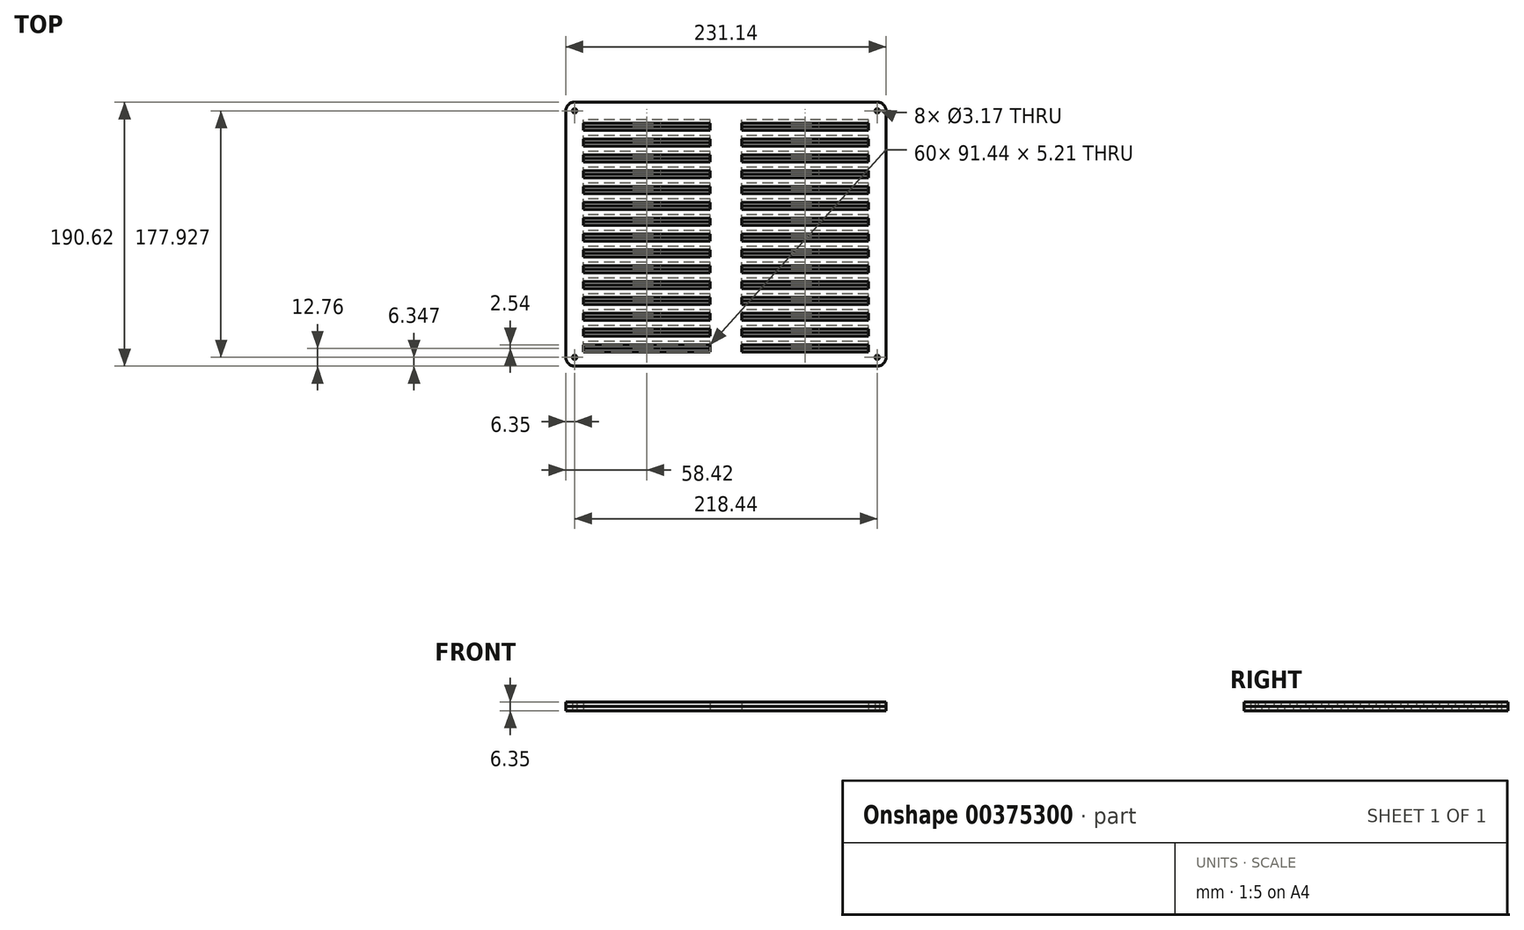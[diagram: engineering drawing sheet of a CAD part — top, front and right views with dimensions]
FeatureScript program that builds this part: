
annotation { "Feature Type Name" : "Feature", "Feature Type Description" : "" }
export const myFeature = defineFeature(function(context is Context, id is Id, definition is map)
    precondition{}
    {
        {
            var Q0;
            Q0=qCreatedBy(makeId("Top.planeOp"),FACE);
            var sketch = newSketch(context, id + "F0", { "sketchPlane" : qUnion([Q0])});
            skLineSegment(sketch, "E0.bottom", {"start": v(45.72, -2.6) * mm, "end": v(-45.72, -2.6) * mm});
            skLineSegment(sketch, "E0.top", {"start": v(45.72, 2.6) * mm, "end": v(-45.72, 2.6) * mm});
            skLineSegment(sketch, "E0.left", {"start": v(45.72, -2.6) * mm, "end": v(45.72, 2.6) * mm});
            skLineSegment(sketch, "E0.right", {"start": v(-45.72, -2.6) * mm, "end": v(-45.72, 2.6) * mm});
            skPoint(sketch, "E0.middle", {"position": v(0, 0) * mm});
            skLineSegment(sketch, "E1", {"start": v(0, 0) * mm, "end": v(0, 156.34) * mm, "construction": true});
            skLineSegment(sketch, "E2", {"start": v(0, 0) * mm, "end": v(0, -142.64) * mm, "construction": true});
            skPoint(sketch, "E3.0.1.0", {"position": v(0, 11.43) * mm});
            skLineSegment(sketch, "E3.0.1.1", {"start": v(45.72, 8.83) * mm, "end": v(-45.72, 8.83) * mm});
            skLineSegment(sketch, "E3.0.1.2", {"start": v(45.72, 14.03) * mm, "end": v(-45.72, 14.03) * mm});
            skLineSegment(sketch, "E3.0.1.3", {"start": v(45.72, 8.83) * mm, "end": v(45.72, 14.03) * mm});
            skLineSegment(sketch, "E3.0.1.4", {"start": v(-45.72, 8.83) * mm, "end": v(-45.72, 14.03) * mm});
            skPoint(sketch, "E3.0.2.0", {"position": v(0, 22.86) * mm});
            skLineSegment(sketch, "E3.0.2.1", {"start": v(45.72, 20.26) * mm, "end": v(-45.72, 20.26) * mm});
            skLineSegment(sketch, "E3.0.2.2", {"start": v(45.72, 25.46) * mm, "end": v(-45.72, 25.46) * mm});
            skLineSegment(sketch, "E3.0.2.3", {"start": v(45.72, 20.26) * mm, "end": v(45.72, 25.46) * mm});
            skLineSegment(sketch, "E3.0.2.4", {"start": v(-45.72, 20.26) * mm, "end": v(-45.72, 25.46) * mm});
            skPoint(sketch, "E3.0.3.0", {"position": v(0, 34.29) * mm});
            skLineSegment(sketch, "E3.0.3.1", {"start": v(45.72, 31.69) * mm, "end": v(-45.72, 31.69) * mm});
            skLineSegment(sketch, "E3.0.3.2", {"start": v(45.72, 36.9) * mm, "end": v(-45.72, 36.9) * mm});
            skLineSegment(sketch, "E3.0.3.3", {"start": v(45.72, 31.69) * mm, "end": v(45.72, 36.9) * mm});
            skLineSegment(sketch, "E3.0.3.4", {"start": v(-45.72, 31.69) * mm, "end": v(-45.72, 36.9) * mm});
            skPoint(sketch, "E3.0.4.0", {"position": v(0, 45.72) * mm});
            skLineSegment(sketch, "E3.0.4.1", {"start": v(45.72, 43.12) * mm, "end": v(-45.72, 43.12) * mm});
            skLineSegment(sketch, "E3.0.4.2", {"start": v(45.72, 48.32) * mm, "end": v(-45.72, 48.32) * mm});
            skLineSegment(sketch, "E3.0.4.3", {"start": v(45.72, 43.12) * mm, "end": v(45.72, 48.32) * mm});
            skLineSegment(sketch, "E3.0.4.4", {"start": v(-45.72, 43.12) * mm, "end": v(-45.72, 48.32) * mm});
            skPoint(sketch, "E3.0.5.0", {"position": v(0, 57.15) * mm});
            skLineSegment(sketch, "E3.0.5.1", {"start": v(45.72, 54.55) * mm, "end": v(-45.72, 54.55) * mm});
            skLineSegment(sketch, "E3.0.5.2", {"start": v(45.72, 59.75) * mm, "end": v(-45.72, 59.75) * mm});
            skLineSegment(sketch, "E3.0.5.3", {"start": v(45.72, 54.55) * mm, "end": v(45.72, 59.75) * mm});
            skLineSegment(sketch, "E3.0.5.4", {"start": v(-45.72, 54.55) * mm, "end": v(-45.72, 59.75) * mm});
            skPoint(sketch, "E3.0.6.0", {"position": v(0, 68.58) * mm});
            skLineSegment(sketch, "E3.0.6.1", {"start": v(45.72, 65.98) * mm, "end": v(-45.72, 65.98) * mm});
            skLineSegment(sketch, "E3.0.6.2", {"start": v(45.72, 71.18) * mm, "end": v(-45.72, 71.18) * mm});
            skLineSegment(sketch, "E3.0.6.3", {"start": v(45.72, 65.98) * mm, "end": v(45.72, 71.18) * mm});
            skLineSegment(sketch, "E3.0.6.4", {"start": v(-45.72, 65.98) * mm, "end": v(-45.72, 71.18) * mm});
            skPoint(sketch, "E3.0.7.0", {"position": v(0, 80) * mm});
            skLineSegment(sketch, "E3.0.7.1", {"start": v(45.72, 77.4) * mm, "end": v(-45.72, 77.4) * mm});
            skLineSegment(sketch, "E3.0.7.2", {"start": v(45.72, 82.61) * mm, "end": v(-45.72, 82.61) * mm});
            skLineSegment(sketch, "E3.0.7.3", {"start": v(45.72, 77.4) * mm, "end": v(45.72, 82.61) * mm});
            skLineSegment(sketch, "E3.0.7.4", {"start": v(-45.72, 77.4) * mm, "end": v(-45.72, 82.61) * mm});
            skPoint(sketch, "E3.0.8.0", {"position": v(0, 91.44) * mm});
            skLineSegment(sketch, "E3.0.8.1", {"start": v(45.72, 88.84) * mm, "end": v(-45.72, 88.84) * mm});
            skLineSegment(sketch, "E3.0.8.2", {"start": v(45.72, 94.04) * mm, "end": v(-45.72, 94.04) * mm});
            skLineSegment(sketch, "E3.0.8.3", {"start": v(45.72, 88.84) * mm, "end": v(45.72, 94.04) * mm});
            skLineSegment(sketch, "E3.0.8.4", {"start": v(-45.72, 88.84) * mm, "end": v(-45.72, 94.04) * mm});
            skPoint(sketch, "E3.0.9.0", {"position": v(0, 102.87) * mm});
            skLineSegment(sketch, "E3.0.9.1", {"start": v(45.72, 100.27) * mm, "end": v(-45.72, 100.27) * mm});
            skLineSegment(sketch, "E3.0.9.2", {"start": v(45.72, 105.47) * mm, "end": v(-45.72, 105.47) * mm});
            skLineSegment(sketch, "E3.0.9.3", {"start": v(45.72, 100.27) * mm, "end": v(45.72, 105.47) * mm});
            skLineSegment(sketch, "E3.0.9.4", {"start": v(-45.72, 100.27) * mm, "end": v(-45.72, 105.47) * mm});
            skPoint(sketch, "E3.0.10.0", {"position": v(0, 114.3) * mm});
            skLineSegment(sketch, "E3.0.10.1", {"start": v(45.72, 111.7) * mm, "end": v(-45.72, 111.7) * mm});
            skLineSegment(sketch, "E3.0.10.2", {"start": v(45.72, 116.9) * mm, "end": v(-45.72, 116.9) * mm});
            skLineSegment(sketch, "E3.0.10.3", {"start": v(45.72, 111.7) * mm, "end": v(45.72, 116.9) * mm});
            skLineSegment(sketch, "E3.0.10.4", {"start": v(-45.72, 111.7) * mm, "end": v(-45.72, 116.9) * mm});
            skPoint(sketch, "E3.0.11.0", {"position": v(0, 125.73) * mm});
            skLineSegment(sketch, "E3.0.11.1", {"start": v(45.72, 123.13) * mm, "end": v(-45.72, 123.13) * mm});
            skLineSegment(sketch, "E3.0.11.2", {"start": v(45.72, 128.33) * mm, "end": v(-45.72, 128.33) * mm});
            skLineSegment(sketch, "E3.0.11.3", {"start": v(45.72, 123.13) * mm, "end": v(45.72, 128.33) * mm});
            skLineSegment(sketch, "E3.0.11.4", {"start": v(-45.72, 123.13) * mm, "end": v(-45.72, 128.33) * mm});
            skPoint(sketch, "E3.0.12.0", {"position": v(0, 137.16) * mm});
            skLineSegment(sketch, "E3.0.12.1", {"start": v(45.72, 134.56) * mm, "end": v(-45.72, 134.56) * mm});
            skLineSegment(sketch, "E3.0.12.2", {"start": v(45.72, 139.76) * mm, "end": v(-45.72, 139.76) * mm});
            skLineSegment(sketch, "E3.0.12.3", {"start": v(45.72, 134.56) * mm, "end": v(45.72, 139.76) * mm});
            skLineSegment(sketch, "E3.0.12.4", {"start": v(-45.72, 134.56) * mm, "end": v(-45.72, 139.76) * mm});
            skPoint(sketch, "E3.0.13.0", {"position": v(0, 148.59) * mm});
            skLineSegment(sketch, "E3.0.13.1", {"start": v(45.72, 145.99) * mm, "end": v(-45.72, 145.99) * mm});
            skLineSegment(sketch, "E3.0.13.2", {"start": v(45.72, 151.2) * mm, "end": v(-45.72, 151.2) * mm});
            skLineSegment(sketch, "E3.0.13.3", {"start": v(45.72, 145.99) * mm, "end": v(45.72, 151.2) * mm});
            skLineSegment(sketch, "E3.0.13.4", {"start": v(-45.72, 145.99) * mm, "end": v(-45.72, 151.2) * mm});
            skPoint(sketch, "E3.0.14.0", {"position": v(0, 160.02) * mm});
            skLineSegment(sketch, "E3.0.14.1", {"start": v(45.72, 157.42) * mm, "end": v(-45.72, 157.42) * mm});
            skLineSegment(sketch, "E3.0.14.2", {"start": v(45.72, 162.62) * mm, "end": v(-45.72, 162.62) * mm});
            skLineSegment(sketch, "E3.0.14.3", {"start": v(45.72, 157.42) * mm, "end": v(45.72, 162.62) * mm});
            skLineSegment(sketch, "E3.0.14.4", {"start": v(-45.72, 157.42) * mm, "end": v(-45.72, 162.62) * mm});
            skPoint(sketch, "E3.1.0.0", {"position": v(114.3, 0) * mm});
            skLineSegment(sketch, "E3.1.0.1", {"start": v(160.02, -2.6) * mm, "end": v(68.58, -2.6) * mm});
            skLineSegment(sketch, "E3.1.0.2", {"start": v(160.02, 2.6) * mm, "end": v(68.58, 2.6) * mm});
            skLineSegment(sketch, "E3.1.0.3", {"start": v(160.02, -2.6) * mm, "end": v(160.02, 2.6) * mm});
            skLineSegment(sketch, "E3.1.0.4", {"start": v(68.58, -2.6) * mm, "end": v(68.58, 2.6) * mm});
            skPoint(sketch, "E3.1.1.0", {"position": v(114.3, 11.43) * mm});
            skLineSegment(sketch, "E3.1.1.1", {"start": v(160.02, 8.83) * mm, "end": v(68.58, 8.83) * mm});
            skLineSegment(sketch, "E3.1.1.2", {"start": v(160.02, 14.03) * mm, "end": v(68.58, 14.03) * mm});
            skLineSegment(sketch, "E3.1.1.3", {"start": v(160.02, 8.83) * mm, "end": v(160.02, 14.03) * mm});
            skLineSegment(sketch, "E3.1.1.4", {"start": v(68.58, 8.83) * mm, "end": v(68.58, 14.03) * mm});
            skPoint(sketch, "E3.1.2.0", {"position": v(114.3, 22.86) * mm});
            skLineSegment(sketch, "E3.1.2.1", {"start": v(160.02, 20.26) * mm, "end": v(68.58, 20.26) * mm});
            skLineSegment(sketch, "E3.1.2.2", {"start": v(160.02, 25.46) * mm, "end": v(68.58, 25.46) * mm});
            skLineSegment(sketch, "E3.1.2.3", {"start": v(160.02, 20.26) * mm, "end": v(160.02, 25.46) * mm});
            skLineSegment(sketch, "E3.1.2.4", {"start": v(68.58, 20.26) * mm, "end": v(68.58, 25.46) * mm});
            skPoint(sketch, "E3.1.3.0", {"position": v(114.3, 34.29) * mm});
            skLineSegment(sketch, "E3.1.3.1", {"start": v(160.02, 31.69) * mm, "end": v(68.58, 31.69) * mm});
            skLineSegment(sketch, "E3.1.3.2", {"start": v(160.02, 36.9) * mm, "end": v(68.58, 36.9) * mm});
            skLineSegment(sketch, "E3.1.3.3", {"start": v(160.02, 31.69) * mm, "end": v(160.02, 36.9) * mm});
            skLineSegment(sketch, "E3.1.3.4", {"start": v(68.58, 31.69) * mm, "end": v(68.58, 36.9) * mm});
            skPoint(sketch, "E3.1.4.0", {"position": v(114.3, 45.72) * mm});
            skLineSegment(sketch, "E3.1.4.1", {"start": v(160.02, 43.12) * mm, "end": v(68.58, 43.12) * mm});
            skLineSegment(sketch, "E3.1.4.2", {"start": v(160.02, 48.32) * mm, "end": v(68.58, 48.32) * mm});
            skLineSegment(sketch, "E3.1.4.3", {"start": v(160.02, 43.12) * mm, "end": v(160.02, 48.32) * mm});
            skLineSegment(sketch, "E3.1.4.4", {"start": v(68.58, 43.12) * mm, "end": v(68.58, 48.32) * mm});
            skPoint(sketch, "E3.1.5.0", {"position": v(114.3, 57.15) * mm});
            skLineSegment(sketch, "E3.1.5.1", {"start": v(160.02, 54.55) * mm, "end": v(68.58, 54.55) * mm});
            skLineSegment(sketch, "E3.1.5.2", {"start": v(160.02, 59.75) * mm, "end": v(68.58, 59.75) * mm});
            skLineSegment(sketch, "E3.1.5.3", {"start": v(160.02, 54.55) * mm, "end": v(160.02, 59.75) * mm});
            skLineSegment(sketch, "E3.1.5.4", {"start": v(68.58, 54.55) * mm, "end": v(68.58, 59.75) * mm});
            skPoint(sketch, "E3.1.6.0", {"position": v(114.3, 68.58) * mm});
            skLineSegment(sketch, "E3.1.6.1", {"start": v(160.02, 65.98) * mm, "end": v(68.58, 65.98) * mm});
            skLineSegment(sketch, "E3.1.6.2", {"start": v(160.02, 71.18) * mm, "end": v(68.58, 71.18) * mm});
            skLineSegment(sketch, "E3.1.6.3", {"start": v(160.02, 65.98) * mm, "end": v(160.02, 71.18) * mm});
            skLineSegment(sketch, "E3.1.6.4", {"start": v(68.58, 65.98) * mm, "end": v(68.58, 71.18) * mm});
            skPoint(sketch, "E3.1.7.0", {"position": v(114.3, 80) * mm});
            skLineSegment(sketch, "E3.1.7.1", {"start": v(160.02, 77.4) * mm, "end": v(68.58, 77.4) * mm});
            skLineSegment(sketch, "E3.1.7.2", {"start": v(160.02, 82.61) * mm, "end": v(68.58, 82.61) * mm});
            skLineSegment(sketch, "E3.1.7.3", {"start": v(160.02, 77.4) * mm, "end": v(160.02, 82.61) * mm});
            skLineSegment(sketch, "E3.1.7.4", {"start": v(68.58, 77.4) * mm, "end": v(68.58, 82.61) * mm});
            skPoint(sketch, "E3.1.8.0", {"position": v(114.3, 91.44) * mm});
            skLineSegment(sketch, "E3.1.8.1", {"start": v(160.02, 88.84) * mm, "end": v(68.58, 88.84) * mm});
            skLineSegment(sketch, "E3.1.8.2", {"start": v(160.02, 94.04) * mm, "end": v(68.58, 94.04) * mm});
            skLineSegment(sketch, "E3.1.8.3", {"start": v(160.02, 88.84) * mm, "end": v(160.02, 94.04) * mm});
            skLineSegment(sketch, "E3.1.8.4", {"start": v(68.58, 88.84) * mm, "end": v(68.58, 94.04) * mm});
            skPoint(sketch, "E3.1.9.0", {"position": v(114.3, 102.87) * mm});
            skLineSegment(sketch, "E3.1.9.1", {"start": v(160.02, 100.27) * mm, "end": v(68.58, 100.27) * mm});
            skLineSegment(sketch, "E3.1.9.2", {"start": v(160.02, 105.47) * mm, "end": v(68.58, 105.47) * mm});
            skLineSegment(sketch, "E3.1.9.3", {"start": v(160.02, 100.27) * mm, "end": v(160.02, 105.47) * mm});
            skLineSegment(sketch, "E3.1.9.4", {"start": v(68.58, 100.27) * mm, "end": v(68.58, 105.47) * mm});
            skPoint(sketch, "E3.1.10.0", {"position": v(114.3, 114.3) * mm});
            skLineSegment(sketch, "E3.1.10.1", {"start": v(160.02, 111.7) * mm, "end": v(68.58, 111.7) * mm});
            skLineSegment(sketch, "E3.1.10.2", {"start": v(160.02, 116.9) * mm, "end": v(68.58, 116.9) * mm});
            skLineSegment(sketch, "E3.1.10.3", {"start": v(160.02, 111.7) * mm, "end": v(160.02, 116.9) * mm});
            skLineSegment(sketch, "E3.1.10.4", {"start": v(68.58, 111.7) * mm, "end": v(68.58, 116.9) * mm});
            skPoint(sketch, "E3.1.11.0", {"position": v(114.3, 125.73) * mm});
            skLineSegment(sketch, "E3.1.11.1", {"start": v(160.02, 123.13) * mm, "end": v(68.58, 123.13) * mm});
            skLineSegment(sketch, "E3.1.11.2", {"start": v(160.02, 128.33) * mm, "end": v(68.58, 128.33) * mm});
            skLineSegment(sketch, "E3.1.11.3", {"start": v(160.02, 123.13) * mm, "end": v(160.02, 128.33) * mm});
            skLineSegment(sketch, "E3.1.11.4", {"start": v(68.58, 123.13) * mm, "end": v(68.58, 128.33) * mm});
            skPoint(sketch, "E3.1.12.0", {"position": v(114.3, 137.16) * mm});
            skLineSegment(sketch, "E3.1.12.1", {"start": v(160.02, 134.56) * mm, "end": v(68.58, 134.56) * mm});
            skLineSegment(sketch, "E3.1.12.2", {"start": v(160.02, 139.76) * mm, "end": v(68.58, 139.76) * mm});
            skLineSegment(sketch, "E3.1.12.3", {"start": v(160.02, 134.56) * mm, "end": v(160.02, 139.76) * mm});
            skLineSegment(sketch, "E3.1.12.4", {"start": v(68.58, 134.56) * mm, "end": v(68.58, 139.76) * mm});
            skPoint(sketch, "E3.1.13.0", {"position": v(114.3, 148.59) * mm});
            skLineSegment(sketch, "E3.1.13.1", {"start": v(160.02, 145.99) * mm, "end": v(68.58, 145.99) * mm});
            skLineSegment(sketch, "E3.1.13.2", {"start": v(160.02, 151.2) * mm, "end": v(68.58, 151.2) * mm});
            skLineSegment(sketch, "E3.1.13.3", {"start": v(160.02, 145.99) * mm, "end": v(160.02, 151.2) * mm});
            skLineSegment(sketch, "E3.1.13.4", {"start": v(68.58, 145.99) * mm, "end": v(68.58, 151.2) * mm});
            skPoint(sketch, "E3.1.14.0", {"position": v(114.3, 160.02) * mm});
            skLineSegment(sketch, "E3.1.14.1", {"start": v(160.02, 157.42) * mm, "end": v(68.58, 157.42) * mm});
            skLineSegment(sketch, "E3.1.14.2", {"start": v(160.02, 162.62) * mm, "end": v(68.58, 162.62) * mm});
            skLineSegment(sketch, "E3.1.14.3", {"start": v(160.02, 157.42) * mm, "end": v(160.02, 162.62) * mm});
            skLineSegment(sketch, "E3.1.14.4", {"start": v(68.58, 157.42) * mm, "end": v(68.58, 162.62) * mm});
            skLineSegment(sketch, "E3.direction1", {"start": v(-45.72, -2.6) * mm, "end": v(68.58, -2.6) * mm, "construction": true});
            skLineSegment(sketch, "E3.direction2", {"start": v(-45.72, -2.6) * mm, "end": v(-45.72, 8.83) * mm, "construction": true});
            skLineSegment(sketch, "E4.bottom", {"start": v(-45.72, -2.6) * mm, "end": v(160.02, -2.6) * mm, "construction": true});
            skLineSegment(sketch, "E4.top", {"start": v(-45.72, 162.62) * mm, "end": v(160.02, 162.62) * mm, "construction": true});
            skLineSegment(sketch, "E4.left", {"start": v(-45.72, -2.6) * mm, "end": v(-45.72, 162.62) * mm, "construction": true});
            skLineSegment(sketch, "E4.right", {"start": v(160.02, -2.6) * mm, "end": v(160.02, 162.62) * mm, "construction": true});
            skLineSegment(sketch, "E5.0", {"start": v(-52.07, 175.32) * mm, "end": v(166.37, 175.32) * mm});
            skLineSegment(sketch, "E5.1", {"start": v(-58.42, -8.95) * mm, "end": v(-58.42, 168.97) * mm});
            skLineSegment(sketch, "E5.2", {"start": v(-52.07, -15.3) * mm, "end": v(166.37, -15.3) * mm});
            skLineSegment(sketch, "E5.3", {"start": v(172.72, -8.95) * mm, "end": v(172.72, 168.97) * mm});
            skPoint(sketch, "E6", {"position": v(57.15, 175.32) * mm});
            skPoint(sketch, "E7", {"position": v(-58.42, 80) * mm});
            skPoint(sketch, "E8.visualSharp", {"position": v(-58.42, 175.32) * mm});
            skArc(sketch, "E8.filletArc", {"start": v(-52.07, 175.32) * mm, "mid": v(-56.56, 173.46) * mm, "end": v(-58.42, 168.97) * mm});
            skPoint(sketch, "E9.visualSharp", {"position": v(172.72, 175.32) * mm});
            skArc(sketch, "E9.filletArc", {"start": v(172.72, 168.97) * mm, "mid": v(170.86, 173.46) * mm, "end": v(166.37, 175.32) * mm});
            skPoint(sketch, "E10.visualSharp", {"position": v(172.72, -15.3) * mm});
            skArc(sketch, "E10.filletArc", {"start": v(166.37, -15.3) * mm, "mid": v(170.86, -13.44) * mm, "end": v(172.72, -8.95) * mm});
            skPoint(sketch, "E11.visualSharp", {"position": v(-58.42, -15.3) * mm});
            skArc(sketch, "E11.filletArc", {"start": v(-58.42, -8.95) * mm, "mid": v(-56.56, -13.44) * mm, "end": v(-52.07, -15.3) * mm});
            skCircle(sketch, "E12", {"center": v(-52.07, 168.97) * mm, "radius": 1.59 * mm});
            skCircle(sketch, "E13", {"center": v(166.37, 168.97) * mm, "radius": 1.59 * mm});
            skCircle(sketch, "E14", {"center": v(166.37, -8.95) * mm, "radius": 1.59 * mm});
            skCircle(sketch, "E15", {"center": v(-52.07, -8.95) * mm, "radius": 1.59 * mm});
            skSolve(sketch);
        }
        {
            var Q0;
            Q0 = qSketchRegion(id + "F0", true);
            extrude(context, id + "F1", {"entities" : qUnion([Q0]), "depth" : 3.17 * mm});
        }
        {
            var Q0;
            Q0=makeQuery(id+"F1.opExtrude","CAP_FACE",FACE,{"disambiguationData":[OSD([sQuery(id+"F0.wireOp",EDGE,"E0.bottom"),sQuery(id+"F0.wireOp",EDGE,"E0.top"),sQuery(id+"F0.wireOp",EDGE,"E0.left"),sQuery(id+"F0.wireOp",EDGE,"E0.right"),sQuery(id+"F0.wireOp",EDGE,"E3.0.1.1"),sQuery(id+"F0.wireOp",EDGE,"E3.0.1.2"),sQuery(id+"F0.wireOp",EDGE,"E3.0.1.3"),sQuery(id+"F0.wireOp",EDGE,"E3.0.1.4"),sQuery(id+"F0.wireOp",EDGE,"E3.0.2.1"),sQuery(id+"F0.wireOp",EDGE,"E3.0.2.2"),sQuery(id+"F0.wireOp",EDGE,"E3.0.2.3"),sQuery(id+"F0.wireOp",EDGE,"E3.0.2.4"),sQuery(id+"F0.wireOp",EDGE,"E3.0.3.1"),sQuery(id+"F0.wireOp",EDGE,"E3.0.3.2"),sQuery(id+"F0.wireOp",EDGE,"E3.0.3.3"),sQuery(id+"F0.wireOp",EDGE,"E3.0.3.4"),sQuery(id+"F0.wireOp",EDGE,"E3.0.4.1"),sQuery(id+"F0.wireOp",EDGE,"E3.0.4.2"),sQuery(id+"F0.wireOp",EDGE,"E3.0.4.3"),sQuery(id+"F0.wireOp",EDGE,"E3.0.4.4"),sQuery(id+"F0.wireOp",EDGE,"E3.0.5.1"),sQuery(id+"F0.wireOp",EDGE,"E3.0.5.2"),sQuery(id+"F0.wireOp",EDGE,"E3.0.5.3"),sQuery(id+"F0.wireOp",EDGE,"E3.0.5.4"),sQuery(id+"F0.wireOp",EDGE,"E3.0.6.1"),sQuery(id+"F0.wireOp",EDGE,"E3.0.6.2"),sQuery(id+"F0.wireOp",EDGE,"E3.0.6.3"),sQuery(id+"F0.wireOp",EDGE,"E3.0.6.4"),sQuery(id+"F0.wireOp",EDGE,"E3.0.7.1"),sQuery(id+"F0.wireOp",EDGE,"E3.0.7.2"),sQuery(id+"F0.wireOp",EDGE,"E3.0.7.3"),sQuery(id+"F0.wireOp",EDGE,"E3.0.7.4"),sQuery(id+"F0.wireOp",EDGE,"E3.0.8.1"),sQuery(id+"F0.wireOp",EDGE,"E3.0.8.2"),sQuery(id+"F0.wireOp",EDGE,"E3.0.8.3"),sQuery(id+"F0.wireOp",EDGE,"E3.0.8.4"),sQuery(id+"F0.wireOp",EDGE,"E3.0.9.1"),sQuery(id+"F0.wireOp",EDGE,"E3.0.9.2"),sQuery(id+"F0.wireOp",EDGE,"E3.0.9.3"),sQuery(id+"F0.wireOp",EDGE,"E3.0.9.4"),sQuery(id+"F0.wireOp",EDGE,"E3.0.10.1"),sQuery(id+"F0.wireOp",EDGE,"E3.0.10.2"),sQuery(id+"F0.wireOp",EDGE,"E3.0.10.3"),sQuery(id+"F0.wireOp",EDGE,"E3.0.10.4"),sQuery(id+"F0.wireOp",EDGE,"E3.0.11.1"),sQuery(id+"F0.wireOp",EDGE,"E3.0.11.2"),sQuery(id+"F0.wireOp",EDGE,"E3.0.11.3"),sQuery(id+"F0.wireOp",EDGE,"E3.0.11.4"),sQuery(id+"F0.wireOp",EDGE,"E3.0.12.1"),sQuery(id+"F0.wireOp",EDGE,"E3.0.12.2"),sQuery(id+"F0.wireOp",EDGE,"E3.0.12.3"),sQuery(id+"F0.wireOp",EDGE,"E3.0.12.4"),sQuery(id+"F0.wireOp",EDGE,"E3.0.13.1"),sQuery(id+"F0.wireOp",EDGE,"E3.0.13.2"),sQuery(id+"F0.wireOp",EDGE,"E3.0.13.3"),sQuery(id+"F0.wireOp",EDGE,"E3.0.13.4"),sQuery(id+"F0.wireOp",EDGE,"E3.0.14.1"),sQuery(id+"F0.wireOp",EDGE,"E3.0.14.2"),sQuery(id+"F0.wireOp",EDGE,"E3.0.14.3"),sQuery(id+"F0.wireOp",EDGE,"E3.0.14.4"),sQuery(id+"F0.wireOp",EDGE,"E3.1.0.1"),sQuery(id+"F0.wireOp",EDGE,"E3.1.0.2"),sQuery(id+"F0.wireOp",EDGE,"E3.1.0.3"),sQuery(id+"F0.wireOp",EDGE,"E3.1.0.4"),sQuery(id+"F0.wireOp",EDGE,"E3.1.1.1"),sQuery(id+"F0.wireOp",EDGE,"E3.1.1.2"),sQuery(id+"F0.wireOp",EDGE,"E3.1.1.3"),sQuery(id+"F0.wireOp",EDGE,"E3.1.1.4"),sQuery(id+"F0.wireOp",EDGE,"E3.1.2.1"),sQuery(id+"F0.wireOp",EDGE,"E3.1.2.2"),sQuery(id+"F0.wireOp",EDGE,"E3.1.2.3"),sQuery(id+"F0.wireOp",EDGE,"E3.1.2.4"),sQuery(id+"F0.wireOp",EDGE,"E3.1.3.1"),sQuery(id+"F0.wireOp",EDGE,"E3.1.3.2"),sQuery(id+"F0.wireOp",EDGE,"E3.1.3.3"),sQuery(id+"F0.wireOp",EDGE,"E3.1.3.4"),sQuery(id+"F0.wireOp",EDGE,"E3.1.4.1"),sQuery(id+"F0.wireOp",EDGE,"E3.1.4.2"),sQuery(id+"F0.wireOp",EDGE,"E3.1.4.3"),sQuery(id+"F0.wireOp",EDGE,"E3.1.4.4"),sQuery(id+"F0.wireOp",EDGE,"E3.1.5.1"),sQuery(id+"F0.wireOp",EDGE,"E3.1.5.2"),sQuery(id+"F0.wireOp",EDGE,"E3.1.5.3"),sQuery(id+"F0.wireOp",EDGE,"E3.1.5.4"),sQuery(id+"F0.wireOp",EDGE,"E3.1.6.1"),sQuery(id+"F0.wireOp",EDGE,"E3.1.6.2"),sQuery(id+"F0.wireOp",EDGE,"E3.1.6.3"),sQuery(id+"F0.wireOp",EDGE,"E3.1.6.4"),sQuery(id+"F0.wireOp",EDGE,"E3.1.7.1"),sQuery(id+"F0.wireOp",EDGE,"E3.1.7.2"),sQuery(id+"F0.wireOp",EDGE,"E3.1.7.3"),sQuery(id+"F0.wireOp",EDGE,"E3.1.7.4"),sQuery(id+"F0.wireOp",EDGE,"E3.1.8.1"),sQuery(id+"F0.wireOp",EDGE,"E3.1.8.2"),sQuery(id+"F0.wireOp",EDGE,"E3.1.8.3"),sQuery(id+"F0.wireOp",EDGE,"E3.1.8.4"),sQuery(id+"F0.wireOp",EDGE,"E3.1.9.1"),sQuery(id+"F0.wireOp",EDGE,"E3.1.9.2"),sQuery(id+"F0.wireOp",EDGE,"E3.1.9.3"),sQuery(id+"F0.wireOp",EDGE,"E3.1.9.4"),sQuery(id+"F0.wireOp",EDGE,"E3.1.10.1"),sQuery(id+"F0.wireOp",EDGE,"E3.1.10.2"),sQuery(id+"F0.wireOp",EDGE,"E3.1.10.3"),sQuery(id+"F0.wireOp",EDGE,"E3.1.10.4"),sQuery(id+"F0.wireOp",EDGE,"E3.1.11.1"),sQuery(id+"F0.wireOp",EDGE,"E3.1.11.2"),sQuery(id+"F0.wireOp",EDGE,"E3.1.11.3"),sQuery(id+"F0.wireOp",EDGE,"E3.1.11.4"),sQuery(id+"F0.wireOp",EDGE,"E3.1.12.1"),sQuery(id+"F0.wireOp",EDGE,"E3.1.12.2"),sQuery(id+"F0.wireOp",EDGE,"E3.1.12.3"),sQuery(id+"F0.wireOp",EDGE,"E3.1.12.4"),sQuery(id+"F0.wireOp",EDGE,"E3.1.13.1"),sQuery(id+"F0.wireOp",EDGE,"E3.1.13.2"),sQuery(id+"F0.wireOp",EDGE,"E3.1.13.3"),sQuery(id+"F0.wireOp",EDGE,"E3.1.13.4"),sQuery(id+"F0.wireOp",EDGE,"E3.1.14.1"),sQuery(id+"F0.wireOp",EDGE,"E3.1.14.2"),sQuery(id+"F0.wireOp",EDGE,"E3.1.14.3"),sQuery(id+"F0.wireOp",EDGE,"E3.1.14.4"),sQuery(id+"F0.wireOp",EDGE,"E5.0"),sQuery(id+"F0.wireOp",EDGE,"E5.1"),sQuery(id+"F0.wireOp",EDGE,"E5.2"),sQuery(id+"F0.wireOp",EDGE,"E5.3"),sQuery(id+"F0.wireOp",EDGE,"E8.filletArc"),sQuery(id+"F0.wireOp",EDGE,"E9.filletArc"),sQuery(id+"F0.wireOp",EDGE,"E10.filletArc"),sQuery(id+"F0.wireOp",EDGE,"E11.filletArc"),sQuery(id+"F0.wireOp",EDGE,"E12"),sQuery(id+"F0.wireOp",EDGE,"E13"),sQuery(id+"F0.wireOp",EDGE,"E14"),sQuery(id+"F0.wireOp",EDGE,"E15")])],"isStart":false});
            var sketch = newSketch(context, id + "F2", { "sketchPlane" : qUnion([Q0])});
            skLineSegment(sketch, "E16.0", {"start": v(172.72, -8.95) * mm, "end": v(172.72, 168.97) * mm});
            skArc(sketch, "E16.1", {"start": v(-52.07, 175.32) * mm, "mid": v(-56.56, 173.46) * mm, "end": v(-58.42, 168.97) * mm});
            skLineSegment(sketch, "E16.2", {"start": v(172.72, -8.95) * mm, "end": v(172.72, 168.97) * mm});
            skCircle(sketch, "E16.3", {"center": v(-52.07, -8.95) * mm, "radius": 1.59 * mm});
            skArc(sketch, "E16.4", {"start": v(-52.07, 175.32) * mm, "mid": v(-56.56, 173.46) * mm, "end": v(-58.42, 168.97) * mm});
            skArc(sketch, "E16.5", {"start": v(172.72, 168.97) * mm, "mid": v(170.86, 173.46) * mm, "end": v(166.37, 175.32) * mm});
            skLineSegment(sketch, "E16.7", {"start": v(-52.07, 175.32) * mm, "end": v(166.37, 175.32) * mm});
            skCircle(sketch, "E16.8", {"center": v(-52.07, 168.97) * mm, "radius": 1.59 * mm});
            skLineSegment(sketch, "E16.9", {"start": v(-52.07, 175.32) * mm, "end": v(166.37, 175.32) * mm});
            skArc(sketch, "E16.10", {"start": v(-58.42, -8.95) * mm, "mid": v(-56.56, -13.44) * mm, "end": v(-52.07, -15.3) * mm});
            skArc(sketch, "E16.11", {"start": v(166.37, -15.3) * mm, "mid": v(170.86, -13.44) * mm, "end": v(172.72, -8.95) * mm});
            skCircle(sketch, "E16.12", {"center": v(166.37, -8.95) * mm, "radius": 1.59 * mm});
            skLineSegment(sketch, "E16.13", {"start": v(-52.07, -15.3) * mm, "end": v(166.37, -15.3) * mm});
            skCircle(sketch, "E16.14", {"center": v(166.37, 168.97) * mm, "radius": 1.59 * mm});
            skLineSegment(sketch, "E16.15", {"start": v(-58.42, -8.95) * mm, "end": v(-58.42, 168.97) * mm});
            skPoint(sketch, "E16.6.end.orphan", {"position": v(68.58, 145.99) * mm});
            skPoint(sketch, "E16.6.start.orphan", {"position": v(160.02, 145.99) * mm});
            skLineSegment(sketch, "E17.bottom", {"start": v(-45.72, -5.14) * mm, "end": v(45.72, -5.14) * mm});
            skLineSegment(sketch, "E17.top", {"start": v(-45.72, 0.06) * mm, "end": v(45.72, 0.06) * mm});
            skLineSegment(sketch, "E17.left", {"start": v(-45.72, -5.14) * mm, "end": v(-45.72, 0.06) * mm});
            skLineSegment(sketch, "E17.right", {"start": v(45.72, -5.14) * mm, "end": v(45.72, 0.06) * mm});
            skPoint(sketch, "E18", {"position": v(0, -2.54) * mm});
            skPoint(sketch, "E18.positionSnap0", {"position": v(45.72, -2.54) * mm});
            skPoint(sketch, "E18.positionSnap1", {"position": v(0, -5.14) * mm});
            skLineSegment(sketch, "E19.0.1.0", {"start": v(-45.72, 6.29) * mm, "end": v(-45.72, 11.5) * mm});
            skLineSegment(sketch, "E19.0.1.1", {"start": v(-45.72, 11.5) * mm, "end": v(45.72, 11.5) * mm});
            skLineSegment(sketch, "E19.0.1.2", {"start": v(-45.72, 6.29) * mm, "end": v(45.72, 6.29) * mm});
            skPoint(sketch, "E19.0.1.3", {"position": v(0, 8.9) * mm});
            skPoint(sketch, "E19.0.1.4", {"position": v(45.72, 8.9) * mm});
            skPoint(sketch, "E19.0.1.5", {"position": v(0, 6.29) * mm});
            skLineSegment(sketch, "E19.0.1.6", {"start": v(45.72, 6.29) * mm, "end": v(45.72, 11.5) * mm});
            skLineSegment(sketch, "E19.0.2.0", {"start": v(-45.72, 17.72) * mm, "end": v(-45.72, 22.92) * mm});
            skLineSegment(sketch, "E19.0.2.1", {"start": v(-45.72, 22.92) * mm, "end": v(45.72, 22.92) * mm});
            skLineSegment(sketch, "E19.0.2.2", {"start": v(-45.72, 17.72) * mm, "end": v(45.72, 17.72) * mm});
            skPoint(sketch, "E19.0.2.3", {"position": v(0, 20.32) * mm});
            skPoint(sketch, "E19.0.2.4", {"position": v(45.72, 20.32) * mm});
            skPoint(sketch, "E19.0.2.5", {"position": v(0, 17.72) * mm});
            skLineSegment(sketch, "E19.0.2.6", {"start": v(45.72, 17.72) * mm, "end": v(45.72, 22.92) * mm});
            skLineSegment(sketch, "E19.0.3.0", {"start": v(-45.72, 29.15) * mm, "end": v(-45.72, 34.35) * mm});
            skLineSegment(sketch, "E19.0.3.1", {"start": v(-45.72, 34.35) * mm, "end": v(45.72, 34.35) * mm});
            skLineSegment(sketch, "E19.0.3.2", {"start": v(-45.72, 29.15) * mm, "end": v(45.72, 29.15) * mm});
            skPoint(sketch, "E19.0.3.3", {"position": v(0, 31.75) * mm});
            skPoint(sketch, "E19.0.3.4", {"position": v(45.72, 31.75) * mm});
            skPoint(sketch, "E19.0.3.5", {"position": v(0, 29.15) * mm});
            skLineSegment(sketch, "E19.0.3.6", {"start": v(45.72, 29.15) * mm, "end": v(45.72, 34.35) * mm});
            skLineSegment(sketch, "E19.0.4.0", {"start": v(-45.72, 40.58) * mm, "end": v(-45.72, 45.78) * mm});
            skLineSegment(sketch, "E19.0.4.1", {"start": v(-45.72, 45.78) * mm, "end": v(45.72, 45.78) * mm});
            skLineSegment(sketch, "E19.0.4.2", {"start": v(-45.72, 40.58) * mm, "end": v(45.72, 40.58) * mm});
            skPoint(sketch, "E19.0.4.3", {"position": v(0, 43.18) * mm});
            skPoint(sketch, "E19.0.4.4", {"position": v(45.72, 43.18) * mm});
            skPoint(sketch, "E19.0.4.5", {"position": v(0, 40.58) * mm});
            skLineSegment(sketch, "E19.0.4.6", {"start": v(45.72, 40.58) * mm, "end": v(45.72, 45.78) * mm});
            skLineSegment(sketch, "E19.0.5.0", {"start": v(-45.72, 52) * mm, "end": v(-45.72, 57.21) * mm});
            skLineSegment(sketch, "E19.0.5.1", {"start": v(-45.72, 57.21) * mm, "end": v(45.72, 57.21) * mm});
            skLineSegment(sketch, "E19.0.5.2", {"start": v(-45.72, 52) * mm, "end": v(45.72, 52) * mm});
            skPoint(sketch, "E19.0.5.3", {"position": v(0, 54.61) * mm});
            skPoint(sketch, "E19.0.5.4", {"position": v(45.72, 54.61) * mm});
            skPoint(sketch, "E19.0.5.5", {"position": v(0, 52) * mm});
            skLineSegment(sketch, "E19.0.5.6", {"start": v(45.72, 52) * mm, "end": v(45.72, 57.21) * mm});
            skLineSegment(sketch, "E19.0.6.0", {"start": v(-45.72, 63.44) * mm, "end": v(-45.72, 68.64) * mm});
            skLineSegment(sketch, "E19.0.6.1", {"start": v(-45.72, 68.64) * mm, "end": v(45.72, 68.64) * mm});
            skLineSegment(sketch, "E19.0.6.2", {"start": v(-45.72, 63.44) * mm, "end": v(45.72, 63.44) * mm});
            skPoint(sketch, "E19.0.6.3", {"position": v(0, 66.04) * mm});
            skPoint(sketch, "E19.0.6.4", {"position": v(45.72, 66.04) * mm});
            skPoint(sketch, "E19.0.6.5", {"position": v(0, 63.44) * mm});
            skLineSegment(sketch, "E19.0.6.6", {"start": v(45.72, 63.44) * mm, "end": v(45.72, 68.64) * mm});
            skLineSegment(sketch, "E19.0.7.0", {"start": v(-45.72, 74.87) * mm, "end": v(-45.72, 80.07) * mm});
            skLineSegment(sketch, "E19.0.7.1", {"start": v(-45.72, 80.07) * mm, "end": v(45.72, 80.07) * mm});
            skLineSegment(sketch, "E19.0.7.2", {"start": v(-45.72, 74.87) * mm, "end": v(45.72, 74.87) * mm});
            skPoint(sketch, "E19.0.7.3", {"position": v(0, 77.47) * mm});
            skPoint(sketch, "E19.0.7.4", {"position": v(45.72, 77.47) * mm});
            skPoint(sketch, "E19.0.7.5", {"position": v(0, 74.87) * mm});
            skLineSegment(sketch, "E19.0.7.6", {"start": v(45.72, 74.87) * mm, "end": v(45.72, 80.07) * mm});
            skLineSegment(sketch, "E19.0.8.0", {"start": v(-45.72, 86.3) * mm, "end": v(-45.72, 91.5) * mm});
            skLineSegment(sketch, "E19.0.8.1", {"start": v(-45.72, 91.5) * mm, "end": v(45.72, 91.5) * mm});
            skLineSegment(sketch, "E19.0.8.2", {"start": v(-45.72, 86.3) * mm, "end": v(45.72, 86.3) * mm});
            skPoint(sketch, "E19.0.8.3", {"position": v(0, 88.9) * mm});
            skPoint(sketch, "E19.0.8.4", {"position": v(45.72, 88.9) * mm});
            skPoint(sketch, "E19.0.8.5", {"position": v(0, 86.3) * mm});
            skLineSegment(sketch, "E19.0.8.6", {"start": v(45.72, 86.3) * mm, "end": v(45.72, 91.5) * mm});
            skLineSegment(sketch, "E19.0.9.0", {"start": v(-45.72, 97.73) * mm, "end": v(-45.72, 102.93) * mm});
            skLineSegment(sketch, "E19.0.9.1", {"start": v(-45.72, 102.93) * mm, "end": v(45.72, 102.93) * mm});
            skLineSegment(sketch, "E19.0.9.2", {"start": v(-45.72, 97.73) * mm, "end": v(45.72, 97.73) * mm});
            skPoint(sketch, "E19.0.9.3", {"position": v(0, 100.33) * mm});
            skPoint(sketch, "E19.0.9.4", {"position": v(45.72, 100.33) * mm});
            skPoint(sketch, "E19.0.9.5", {"position": v(0, 97.73) * mm});
            skLineSegment(sketch, "E19.0.9.6", {"start": v(45.72, 97.73) * mm, "end": v(45.72, 102.93) * mm});
            skLineSegment(sketch, "E19.0.10.0", {"start": v(-45.72, 109.16) * mm, "end": v(-45.72, 114.36) * mm});
            skLineSegment(sketch, "E19.0.10.1", {"start": v(-45.72, 114.36) * mm, "end": v(45.72, 114.36) * mm});
            skLineSegment(sketch, "E19.0.10.2", {"start": v(-45.72, 109.16) * mm, "end": v(45.72, 109.16) * mm});
            skPoint(sketch, "E19.0.10.3", {"position": v(0, 111.76) * mm});
            skPoint(sketch, "E19.0.10.4", {"position": v(45.72, 111.76) * mm});
            skPoint(sketch, "E19.0.10.5", {"position": v(0, 109.16) * mm});
            skLineSegment(sketch, "E19.0.10.6", {"start": v(45.72, 109.16) * mm, "end": v(45.72, 114.36) * mm});
            skLineSegment(sketch, "E19.0.11.0", {"start": v(-45.72, 120.59) * mm, "end": v(-45.72, 125.8) * mm});
            skLineSegment(sketch, "E19.0.11.1", {"start": v(-45.72, 125.8) * mm, "end": v(45.72, 125.8) * mm});
            skLineSegment(sketch, "E19.0.11.2", {"start": v(-45.72, 120.59) * mm, "end": v(45.72, 120.59) * mm});
            skPoint(sketch, "E19.0.11.3", {"position": v(0, 123.2) * mm});
            skPoint(sketch, "E19.0.11.4", {"position": v(45.72, 123.2) * mm});
            skPoint(sketch, "E19.0.11.5", {"position": v(0, 120.59) * mm});
            skLineSegment(sketch, "E19.0.11.6", {"start": v(45.72, 120.59) * mm, "end": v(45.72, 125.8) * mm});
            skLineSegment(sketch, "E19.0.12.0", {"start": v(-45.72, 132.02) * mm, "end": v(-45.72, 137.22) * mm});
            skLineSegment(sketch, "E19.0.12.1", {"start": v(-45.72, 137.22) * mm, "end": v(45.72, 137.22) * mm});
            skLineSegment(sketch, "E19.0.12.2", {"start": v(-45.72, 132.02) * mm, "end": v(45.72, 132.02) * mm});
            skPoint(sketch, "E19.0.12.3", {"position": v(0, 134.62) * mm});
            skPoint(sketch, "E19.0.12.4", {"position": v(45.72, 134.62) * mm});
            skPoint(sketch, "E19.0.12.5", {"position": v(0, 132.02) * mm});
            skLineSegment(sketch, "E19.0.12.6", {"start": v(45.72, 132.02) * mm, "end": v(45.72, 137.22) * mm});
            skLineSegment(sketch, "E19.0.13.0", {"start": v(-45.72, 143.45) * mm, "end": v(-45.72, 148.65) * mm});
            skLineSegment(sketch, "E19.0.13.1", {"start": v(-45.72, 148.65) * mm, "end": v(45.72, 148.65) * mm});
            skLineSegment(sketch, "E19.0.13.2", {"start": v(-45.72, 143.45) * mm, "end": v(45.72, 143.45) * mm});
            skPoint(sketch, "E19.0.13.3", {"position": v(0, 146.05) * mm});
            skPoint(sketch, "E19.0.13.4", {"position": v(45.72, 146.05) * mm});
            skPoint(sketch, "E19.0.13.5", {"position": v(0, 143.45) * mm});
            skLineSegment(sketch, "E19.0.13.6", {"start": v(45.72, 143.45) * mm, "end": v(45.72, 148.65) * mm});
            skLineSegment(sketch, "E19.0.14.0", {"start": v(-45.72, 154.88) * mm, "end": v(-45.72, 160.08) * mm});
            skLineSegment(sketch, "E19.0.14.1", {"start": v(-45.72, 160.08) * mm, "end": v(45.72, 160.08) * mm});
            skLineSegment(sketch, "E19.0.14.2", {"start": v(-45.72, 154.88) * mm, "end": v(45.72, 154.88) * mm});
            skPoint(sketch, "E19.0.14.3", {"position": v(0, 157.48) * mm});
            skPoint(sketch, "E19.0.14.4", {"position": v(45.72, 157.48) * mm});
            skPoint(sketch, "E19.0.14.5", {"position": v(0, 154.88) * mm});
            skLineSegment(sketch, "E19.0.14.6", {"start": v(45.72, 154.88) * mm, "end": v(45.72, 160.08) * mm});
            skLineSegment(sketch, "E19.1.0.0", {"start": v(68.58, -5.14) * mm, "end": v(68.58, 0.06) * mm});
            skLineSegment(sketch, "E19.1.0.1", {"start": v(68.58, 0.06) * mm, "end": v(160.02, 0.06) * mm});
            skLineSegment(sketch, "E19.1.0.2", {"start": v(68.58, -5.14) * mm, "end": v(160.02, -5.14) * mm});
            skPoint(sketch, "E19.1.0.3", {"position": v(114.3, -2.54) * mm});
            skPoint(sketch, "E19.1.0.4", {"position": v(160.02, -2.54) * mm});
            skPoint(sketch, "E19.1.0.5", {"position": v(114.3, -5.14) * mm});
            skLineSegment(sketch, "E19.1.0.6", {"start": v(160.02, -5.14) * mm, "end": v(160.02, 0.06) * mm});
            skLineSegment(sketch, "E19.1.1.0", {"start": v(68.58, 6.29) * mm, "end": v(68.58, 11.5) * mm});
            skLineSegment(sketch, "E19.1.1.1", {"start": v(68.58, 11.5) * mm, "end": v(160.02, 11.5) * mm});
            skLineSegment(sketch, "E19.1.1.2", {"start": v(68.58, 6.29) * mm, "end": v(160.02, 6.29) * mm});
            skPoint(sketch, "E19.1.1.3", {"position": v(114.3, 8.9) * mm});
            skPoint(sketch, "E19.1.1.4", {"position": v(160.02, 8.9) * mm});
            skPoint(sketch, "E19.1.1.5", {"position": v(114.3, 6.29) * mm});
            skLineSegment(sketch, "E19.1.1.6", {"start": v(160.02, 6.29) * mm, "end": v(160.02, 11.5) * mm});
            skLineSegment(sketch, "E19.1.2.0", {"start": v(68.58, 17.72) * mm, "end": v(68.58, 22.92) * mm});
            skLineSegment(sketch, "E19.1.2.1", {"start": v(68.58, 22.92) * mm, "end": v(160.02, 22.92) * mm});
            skLineSegment(sketch, "E19.1.2.2", {"start": v(68.58, 17.72) * mm, "end": v(160.02, 17.72) * mm});
            skPoint(sketch, "E19.1.2.3", {"position": v(114.3, 20.32) * mm});
            skPoint(sketch, "E19.1.2.4", {"position": v(160.02, 20.32) * mm});
            skPoint(sketch, "E19.1.2.5", {"position": v(114.3, 17.72) * mm});
            skLineSegment(sketch, "E19.1.2.6", {"start": v(160.02, 17.72) * mm, "end": v(160.02, 22.92) * mm});
            skLineSegment(sketch, "E19.1.3.0", {"start": v(68.58, 29.15) * mm, "end": v(68.58, 34.35) * mm});
            skLineSegment(sketch, "E19.1.3.1", {"start": v(68.58, 34.35) * mm, "end": v(160.02, 34.35) * mm});
            skLineSegment(sketch, "E19.1.3.2", {"start": v(68.58, 29.15) * mm, "end": v(160.02, 29.15) * mm});
            skPoint(sketch, "E19.1.3.3", {"position": v(114.3, 31.75) * mm});
            skPoint(sketch, "E19.1.3.4", {"position": v(160.02, 31.75) * mm});
            skPoint(sketch, "E19.1.3.5", {"position": v(114.3, 29.15) * mm});
            skLineSegment(sketch, "E19.1.3.6", {"start": v(160.02, 29.15) * mm, "end": v(160.02, 34.35) * mm});
            skLineSegment(sketch, "E19.1.4.0", {"start": v(68.58, 40.58) * mm, "end": v(68.58, 45.78) * mm});
            skLineSegment(sketch, "E19.1.4.1", {"start": v(68.58, 45.78) * mm, "end": v(160.02, 45.78) * mm});
            skLineSegment(sketch, "E19.1.4.2", {"start": v(68.58, 40.58) * mm, "end": v(160.02, 40.58) * mm});
            skPoint(sketch, "E19.1.4.3", {"position": v(114.3, 43.18) * mm});
            skPoint(sketch, "E19.1.4.4", {"position": v(160.02, 43.18) * mm});
            skPoint(sketch, "E19.1.4.5", {"position": v(114.3, 40.58) * mm});
            skLineSegment(sketch, "E19.1.4.6", {"start": v(160.02, 40.58) * mm, "end": v(160.02, 45.78) * mm});
            skLineSegment(sketch, "E19.1.5.0", {"start": v(68.58, 52) * mm, "end": v(68.58, 57.21) * mm});
            skLineSegment(sketch, "E19.1.5.1", {"start": v(68.58, 57.21) * mm, "end": v(160.02, 57.21) * mm});
            skLineSegment(sketch, "E19.1.5.2", {"start": v(68.58, 52) * mm, "end": v(160.02, 52) * mm});
            skPoint(sketch, "E19.1.5.3", {"position": v(114.3, 54.61) * mm});
            skPoint(sketch, "E19.1.5.4", {"position": v(160.02, 54.61) * mm});
            skPoint(sketch, "E19.1.5.5", {"position": v(114.3, 52) * mm});
            skLineSegment(sketch, "E19.1.5.6", {"start": v(160.02, 52) * mm, "end": v(160.02, 57.21) * mm});
            skLineSegment(sketch, "E19.1.6.0", {"start": v(68.58, 63.44) * mm, "end": v(68.58, 68.64) * mm});
            skLineSegment(sketch, "E19.1.6.1", {"start": v(68.58, 68.64) * mm, "end": v(160.02, 68.64) * mm});
            skLineSegment(sketch, "E19.1.6.2", {"start": v(68.58, 63.44) * mm, "end": v(160.02, 63.44) * mm});
            skPoint(sketch, "E19.1.6.3", {"position": v(114.3, 66.04) * mm});
            skPoint(sketch, "E19.1.6.4", {"position": v(160.02, 66.04) * mm});
            skPoint(sketch, "E19.1.6.5", {"position": v(114.3, 63.44) * mm});
            skLineSegment(sketch, "E19.1.6.6", {"start": v(160.02, 63.44) * mm, "end": v(160.02, 68.64) * mm});
            skLineSegment(sketch, "E19.1.7.0", {"start": v(68.58, 74.87) * mm, "end": v(68.58, 80.07) * mm});
            skLineSegment(sketch, "E19.1.7.1", {"start": v(68.58, 80.07) * mm, "end": v(160.02, 80.07) * mm});
            skLineSegment(sketch, "E19.1.7.2", {"start": v(68.58, 74.87) * mm, "end": v(160.02, 74.87) * mm});
            skPoint(sketch, "E19.1.7.3", {"position": v(114.3, 77.47) * mm});
            skPoint(sketch, "E19.1.7.4", {"position": v(160.02, 77.47) * mm});
            skPoint(sketch, "E19.1.7.5", {"position": v(114.3, 74.87) * mm});
            skLineSegment(sketch, "E19.1.7.6", {"start": v(160.02, 74.87) * mm, "end": v(160.02, 80.07) * mm});
            skLineSegment(sketch, "E19.1.8.0", {"start": v(68.58, 86.3) * mm, "end": v(68.58, 91.5) * mm});
            skLineSegment(sketch, "E19.1.8.1", {"start": v(68.58, 91.5) * mm, "end": v(160.02, 91.5) * mm});
            skLineSegment(sketch, "E19.1.8.2", {"start": v(68.58, 86.3) * mm, "end": v(160.02, 86.3) * mm});
            skPoint(sketch, "E19.1.8.3", {"position": v(114.3, 88.9) * mm});
            skPoint(sketch, "E19.1.8.4", {"position": v(160.02, 88.9) * mm});
            skPoint(sketch, "E19.1.8.5", {"position": v(114.3, 86.3) * mm});
            skLineSegment(sketch, "E19.1.8.6", {"start": v(160.02, 86.3) * mm, "end": v(160.02, 91.5) * mm});
            skLineSegment(sketch, "E19.1.9.0", {"start": v(68.58, 97.73) * mm, "end": v(68.58, 102.93) * mm});
            skLineSegment(sketch, "E19.1.9.1", {"start": v(68.58, 102.93) * mm, "end": v(160.02, 102.93) * mm});
            skLineSegment(sketch, "E19.1.9.2", {"start": v(68.58, 97.73) * mm, "end": v(160.02, 97.73) * mm});
            skPoint(sketch, "E19.1.9.3", {"position": v(114.3, 100.33) * mm});
            skPoint(sketch, "E19.1.9.4", {"position": v(160.02, 100.33) * mm});
            skPoint(sketch, "E19.1.9.5", {"position": v(114.3, 97.73) * mm});
            skLineSegment(sketch, "E19.1.9.6", {"start": v(160.02, 97.73) * mm, "end": v(160.02, 102.93) * mm});
            skLineSegment(sketch, "E19.1.10.0", {"start": v(68.58, 109.16) * mm, "end": v(68.58, 114.36) * mm});
            skLineSegment(sketch, "E19.1.10.1", {"start": v(68.58, 114.36) * mm, "end": v(160.02, 114.36) * mm});
            skLineSegment(sketch, "E19.1.10.2", {"start": v(68.58, 109.16) * mm, "end": v(160.02, 109.16) * mm});
            skPoint(sketch, "E19.1.10.3", {"position": v(114.3, 111.76) * mm});
            skPoint(sketch, "E19.1.10.4", {"position": v(160.02, 111.76) * mm});
            skPoint(sketch, "E19.1.10.5", {"position": v(114.3, 109.16) * mm});
            skLineSegment(sketch, "E19.1.10.6", {"start": v(160.02, 109.16) * mm, "end": v(160.02, 114.36) * mm});
            skLineSegment(sketch, "E19.1.11.0", {"start": v(68.58, 120.59) * mm, "end": v(68.58, 125.8) * mm});
            skLineSegment(sketch, "E19.1.11.1", {"start": v(68.58, 125.8) * mm, "end": v(160.02, 125.8) * mm});
            skLineSegment(sketch, "E19.1.11.2", {"start": v(68.58, 120.59) * mm, "end": v(160.02, 120.59) * mm});
            skPoint(sketch, "E19.1.11.3", {"position": v(114.3, 123.2) * mm});
            skPoint(sketch, "E19.1.11.4", {"position": v(160.02, 123.2) * mm});
            skPoint(sketch, "E19.1.11.5", {"position": v(114.3, 120.59) * mm});
            skLineSegment(sketch, "E19.1.11.6", {"start": v(160.02, 120.59) * mm, "end": v(160.02, 125.8) * mm});
            skLineSegment(sketch, "E19.1.12.0", {"start": v(68.58, 132.02) * mm, "end": v(68.58, 137.22) * mm});
            skLineSegment(sketch, "E19.1.12.1", {"start": v(68.58, 137.22) * mm, "end": v(160.02, 137.22) * mm});
            skLineSegment(sketch, "E19.1.12.2", {"start": v(68.58, 132.02) * mm, "end": v(160.02, 132.02) * mm});
            skPoint(sketch, "E19.1.12.3", {"position": v(114.3, 134.62) * mm});
            skPoint(sketch, "E19.1.12.4", {"position": v(160.02, 134.62) * mm});
            skPoint(sketch, "E19.1.12.5", {"position": v(114.3, 132.02) * mm});
            skLineSegment(sketch, "E19.1.12.6", {"start": v(160.02, 132.02) * mm, "end": v(160.02, 137.22) * mm});
            skLineSegment(sketch, "E19.1.13.0", {"start": v(68.58, 143.45) * mm, "end": v(68.58, 148.65) * mm});
            skLineSegment(sketch, "E19.1.13.1", {"start": v(68.58, 148.65) * mm, "end": v(160.02, 148.65) * mm});
            skLineSegment(sketch, "E19.1.13.2", {"start": v(68.58, 143.45) * mm, "end": v(160.02, 143.45) * mm});
            skPoint(sketch, "E19.1.13.3", {"position": v(114.3, 146.05) * mm});
            skPoint(sketch, "E19.1.13.4", {"position": v(160.02, 146.05) * mm});
            skPoint(sketch, "E19.1.13.5", {"position": v(114.3, 143.45) * mm});
            skLineSegment(sketch, "E19.1.13.6", {"start": v(160.02, 143.45) * mm, "end": v(160.02, 148.65) * mm});
            skLineSegment(sketch, "E19.1.14.0", {"start": v(68.58, 154.88) * mm, "end": v(68.58, 160.08) * mm});
            skLineSegment(sketch, "E19.1.14.1", {"start": v(68.58, 160.08) * mm, "end": v(160.02, 160.08) * mm});
            skLineSegment(sketch, "E19.1.14.2", {"start": v(68.58, 154.88) * mm, "end": v(160.02, 154.88) * mm});
            skPoint(sketch, "E19.1.14.3", {"position": v(114.3, 157.48) * mm});
            skPoint(sketch, "E19.1.14.4", {"position": v(160.02, 157.48) * mm});
            skPoint(sketch, "E19.1.14.5", {"position": v(114.3, 154.88) * mm});
            skLineSegment(sketch, "E19.1.14.6", {"start": v(160.02, 154.88) * mm, "end": v(160.02, 160.08) * mm});
            skLineSegment(sketch, "E19.direction1", {"start": v(-45.72, -5.14) * mm, "end": v(68.58, -5.14) * mm, "construction": true});
            skLineSegment(sketch, "E19.direction2", {"start": v(-45.72, -5.14) * mm, "end": v(-45.72, 6.29) * mm, "construction": true});
            skSolve(sketch);
        }
        {
            var Q0;
            Q0 = qSketchRegion(id + "F2", true);
            extrude(context, id + "F3", {"entities" : qUnion([Q0]), "depth" : 3.17 * mm});
        }
    });
